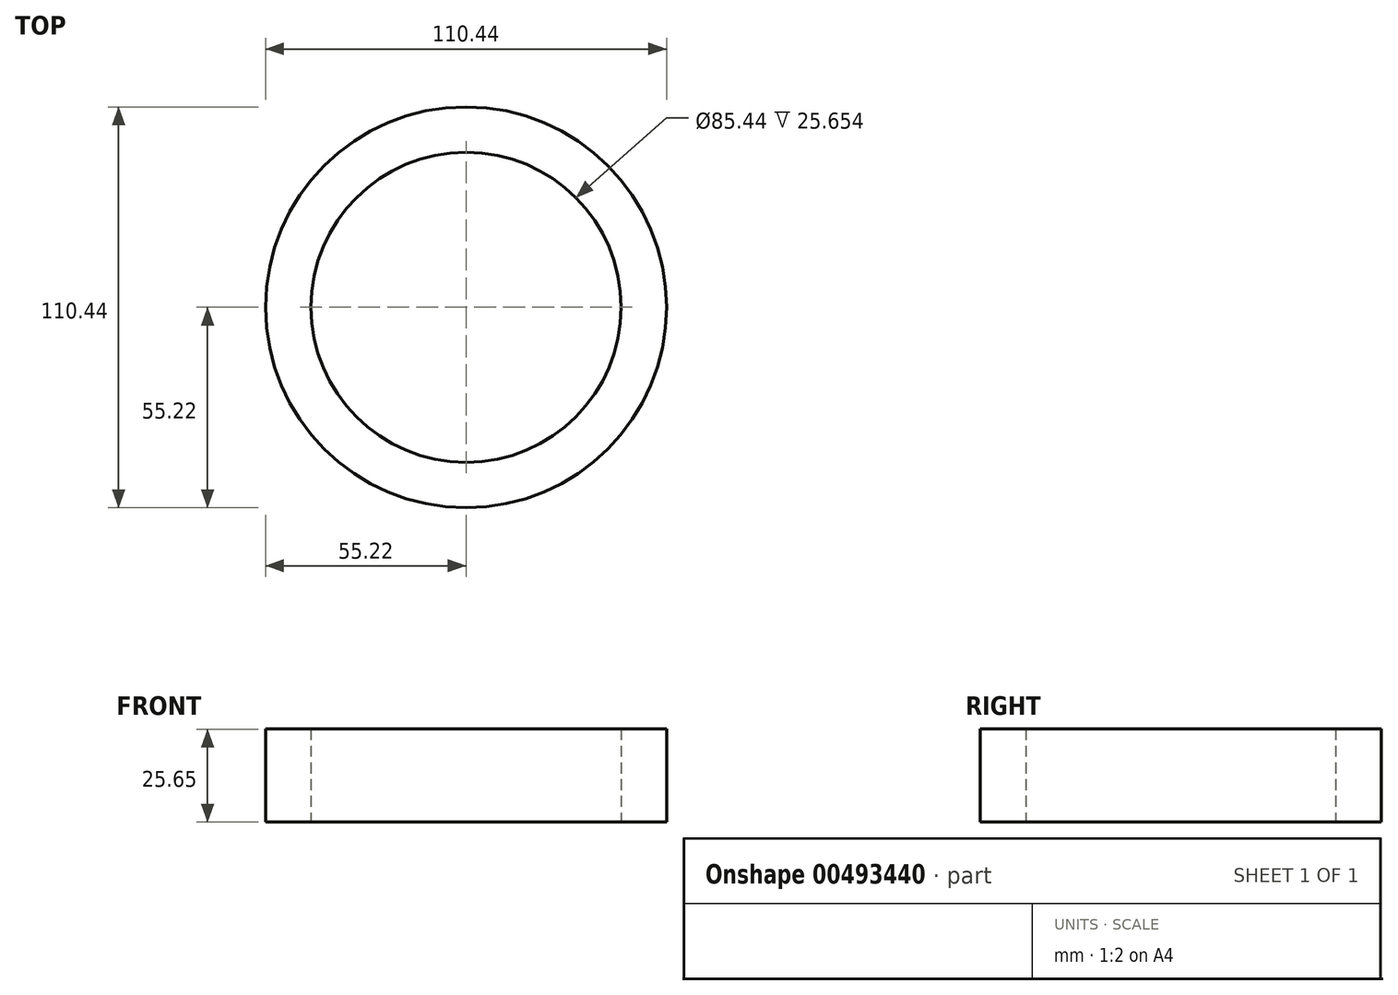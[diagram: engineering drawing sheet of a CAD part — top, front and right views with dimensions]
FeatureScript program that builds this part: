
annotation { "Feature Type Name" : "Feature", "Feature Type Description" : "" }
export const myFeature = defineFeature(function(context is Context, id is Id, definition is map)
    precondition{}
    {
        {
            var Q0;
            Q0=qCreatedBy(makeId("Top.planeOp"),FACE);
            var sketch = newSketch(context, id + "F0", { "sketchPlane" : qUnion([Q0])});
            skCircle(sketch, "E0", {"center": v(0, 0) * mm, "radius": 55.22 * mm});
            skCircle(sketch, "E1", {"center": v(0, 0) * mm, "radius": 42.72 * mm});
            skSolve(sketch);
        }
        {
            var Q0;
            Q0=makeQuery(id+"F0.imprint","IMPRINT",FACE,{"disambiguationData":[TD([[makeQuery(id+"F0.imprint","IMPRINT",EDGE,{"derivedFrom":sQuery(id+"F0.wireOp",EDGE,"E0")}),1.0]])]});
            extrude(context, id + "F1", {"entities" : qUnion([Q0]), "depth" : 25.65 * mm});
        }
    });
